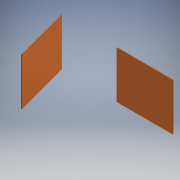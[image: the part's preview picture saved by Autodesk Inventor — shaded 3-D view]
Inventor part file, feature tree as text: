
AUTODESK INVENTOR PART (.ipt)
format: ipt  version: 2016 (Build 200138000, 138)  size: 167,936 bytes
history: native  units: mm
features: extrude x3, sketch x3, projected_geometry x1
ambient origin geometry x8: Origin, YZ Plane, XZ Plane, XY Plane, X Axis, Y Axis, Z Axis, Center Point
bodies: Solid1 (feature_tree)
feature tree (7):
  extrude  "Extrusion1"  Depth=50.0mm
  extrude  "Extrusión10"  Depth=6.0mm
  extrude  "Extrusión11"  TaperAngle=0.0deg  [1 undecoded]
  sketch  "Sketch1"  dims[d2=41.0mm d3=50.0mm]
  sketch  "Boceto10"  dims[d4=100.0mm d5=6.0mm]
  sketch  "Boceto11"  dims[d6=6.0mm d8=0.0mm d49=1180.0mm d50=1180.0mm d52=10.0mm d53=1180.0mm d54=820.0mm d55=0.0mm d56=41.0mm d57=50.0mm d58=100.0mm d59=6.0mm d60=6.0mm d61=820.0mm d62=0.0mm]
  projected_geometry  "Contorno proyectado8"
note: 1 required parameter value undecoded (feature->parameter linkage not recoverable at this tier; creation-order binding heuristic only, values carry confidence <= 0.55)
